# Revit family: 3004 15_Anschlussverschraubung (Ausgleichsadapter)
name_source: partatom
category: Rohrformteile
units: mm (PartAtom-declared; Revit-internal decimal feet)

## family parameters
Arbeitsebenenbasiert = Nein
Beim Laden mit Abzugskörper schneiden = Nein
Bemaßung runder Anschluss = Durchmesser verwenden
Gemeinsam genutzt = Nein
Immer vertikal = Ja
OmniClass-Nummer = 23.65.55.14
OmniClass-Titel = Valves for Liquid Services
Teiletyp = Verbindung

## types (1)
- G3/4
    Anschlussboden = Messing CC754S, vernickelt
    Ausführung = Ausgleichsadapter, Set 2 Stück, zum Ausgleich unterschiedlicher Rohranschlüsse, Radius 15mm, Ventilanschluss 3/4" mit Konus, freidrehende Überwurfmutter konisch dichtend, Rohranschluss 3/4 AG.
    D00 = 16.5 mm  [stored 0.0541339 ft]
    D01 = 10 mm  [stored 0.0328084 ft]
    D02 = 10.2 mm  [stored 0.0334646 ft]
    D03 = 11.1 mm  [stored 0.0364173 ft]
    GT = 7 mm  [stored 0.0229659 ft]
    GT1 = 7.5 mm  [stored 0.0246063 ft]
    Hersteller = HERZ Armaturen Ges.m.b.H.
    Hinweiß = Der O-Ring dient als zusätzliche Dichtung, bei Verlust ist der Ausgleichsadapter metallisch dichtend.
    L01 = 13 mm
    L02 = 3 mm  [stored 0.00984252 ft]
    L03 = 3 mm  [stored 0.00984252 ft]
    L04 = 6.6 mm  [stored 0.0216535 ft]
    L05 = 2.1 mm  [stored 0.00688976 ft]
    L06 = 10 mm  [stored 0.0328084 ft]
    Max. Betriebsdruck = 1000000.0 Pa
    Max. Betriebstemperatur = 110 °C
    Medium = Heizungswasser nach ÖNORM H5195 oder VDI- Richtlinie 2035.
Die Verwendung von Ethylen- oder Propyleneglykol in einem Mischungsverhältnis 25- 50% ist zulässig.
    Mutter = Messing CW614N, vernickelt
    Nennweite_AG = 20 mm  [stored 0.0656168 ft]
    Nennweite_IG = 20 mm  [stored 0.0656168 ft]
    O-Ring = EPDM
    R01 = 15 mm  [stored 0.0492126 ft]
    SCRNCODE = 07;01;02
    SCRNSEQ = AWI;AWI_TYP="1001";2
    URL = www.herz-armaturen.at
    Vorgabe-Ansicht = 0 mm  [stored 0 ft]

note: [stored X ft] marks values corroborated as IEEE doubles in the binary element streams (Revit-internal decimal feet)
